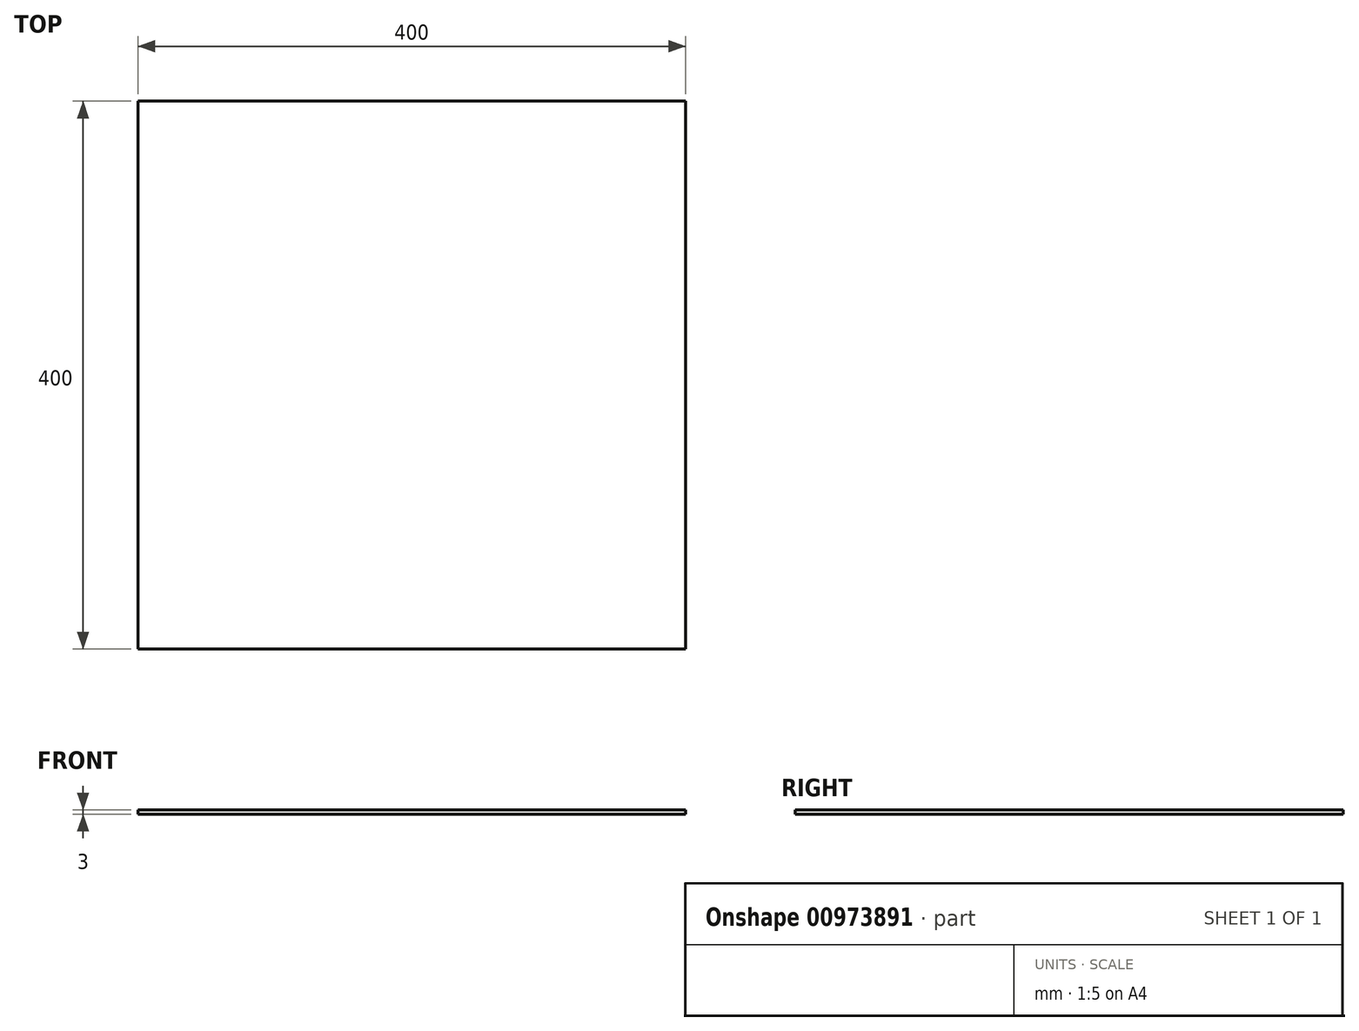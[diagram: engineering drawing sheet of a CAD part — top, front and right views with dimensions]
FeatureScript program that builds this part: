
annotation { "Feature Type Name" : "Feature", "Feature Type Description" : "" }
export const myFeature = defineFeature(function(context is Context, id is Id, definition is map)
    precondition{}
    {
        {
            var Q0;
            Q0=qCreatedBy(makeId("Top.planeOp"),FACE);
            var sketch = newSketch(context, id + "F0", { "sketchPlane" : qUnion([Q0])});
            skLineSegment(sketch, "E0.bottom", {"start": v(-200, 200) * mm, "end": v(200, 200) * mm});
            skLineSegment(sketch, "E0.top", {"start": v(-200, -200) * mm, "end": v(200, -200) * mm});
            skLineSegment(sketch, "E0.left", {"start": v(-200, 200) * mm, "end": v(-200, -200) * mm});
            skLineSegment(sketch, "E0.right", {"start": v(200, 200) * mm, "end": v(200, -200) * mm});
            skLineSegment(sketch, "E1", {"start": v(0, 0) * mm, "end": v(200, -200) * mm, "construction": true});
            skLineSegment(sketch, "E2", {"start": v(200, 200) * mm, "end": v(-200, -200) * mm, "construction": true});
            skSolve(sketch);
        }
        {
            var Q0;
            Q0 = qSketchRegion(id + "F0", true);
            extrude(context, id + "F1", {"entities" : qUnion([Q0]), "depth" : 3 * mm, "offsetDistance" : 25 * mm});
        }
    });
